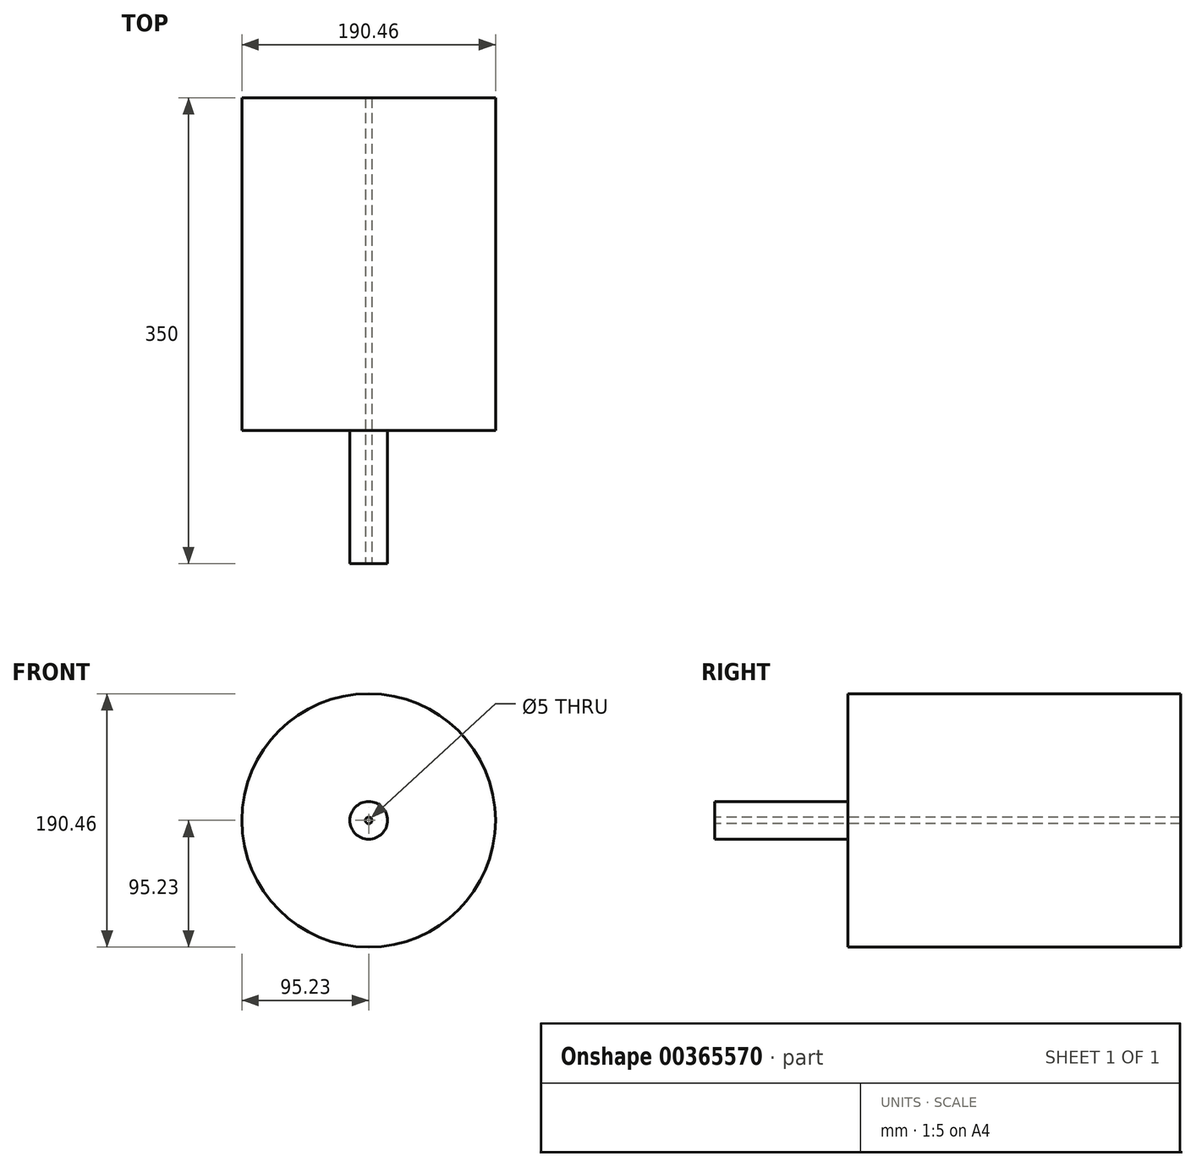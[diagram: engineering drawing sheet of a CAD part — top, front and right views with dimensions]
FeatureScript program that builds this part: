
annotation { "Feature Type Name" : "Feature", "Feature Type Description" : "" }
export const myFeature = defineFeature(function(context is Context, id is Id, definition is map)
    precondition{}
    {
        {
            var Q0;
            Q0=qCreatedBy(makeId("Front.planeOp"),FACE);
            var sketch = newSketch(context, id + "F0", { "sketchPlane" : qUnion([Q0])});
            skCircle(sketch, "E0", {"center": v(0, 0) * mm, "radius": 95.23 * mm});
            skSolve(sketch);
        }
        {
            var Q0;
            Q0 = qSketchRegion(id + "F0", true);
            extrude(context, id + "F1", {"entities" : qUnion([Q0]), "depth" : 50 * mm});
        }
        {
            var Q0;
            Q0=makeQuery(id+"F1.opExtrude","CAP_FACE",FACE,{"disambiguationData":[OSD([sQuery(id+"F0.wireOp",EDGE,"E0")])],"isStart":false});
            var sketch = newSketch(context, id + "F2", { "sketchPlane" : qUnion([Q0])});
            skCircle(sketch, "E1", {"center": v(0, 0) * mm, "radius": 14.1 * mm});
            skSolve(sketch);
        }
        {
            var Q0;
            Q0 = qSketchRegion(id + "F2", true);
            extrude(context, id + "F3", {"entities" : qUnion([Q0]), "operationType" : NewBodyOperationType.ADD, "depth" : 100 * mm});
        }
        {
            var Q0;
            Q0=makeQuery(id+"F1.opExtrude","CAP_FACE",FACE,{"disambiguationData":[OSD([sQuery(id+"F0.wireOp",EDGE,"E0")])],"isStart":true});
            extrude(context, id + "F4", {"entities" : qUnion([Q0]), "operationType" : NewBodyOperationType.ADD, "depth" : 200 * mm});
        }
        {
            var Q0;
            Q0=makeQuery(id+"F3.opExtrude","CAP_FACE",FACE,{"disambiguationData":[OSD([sQuery(id+"F2.wireOp",EDGE,"E1")])],"isStart":false});
            var sketch = newSketch(context, id + "F5", { "sketchPlane" : qUnion([Q0])});
            skPoint(sketch, "E2", {"position": v(0, 0) * mm});
            skSolve(sketch);
        }
        {
            var Q0;
            Q0=sQuery(id+"F5.wireOp",VERTEX,"E2");
            var Q1;
            Q1=makeQuery(id+"F1.opExtrude","SWEPT_BODY",BODY,{"disambiguationData":[OSD([sQuery(id+"F0.wireOp",EDGE,"E0")])]});
            hole(context, id + "F6", {"style" : HoleStyle.SIMPLE, "endStyle" : HoleEndStyle.THROUGH, "holeDiameter" : 5 * mm, "isTappedThrough" : true, "tappedDepth" : 12 * mm, "tapClearance" : 3, "locations" : qUnion([Q0]), "scope" : qUnion([Q1])});
        }
    });
